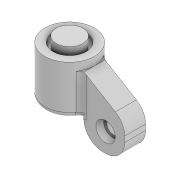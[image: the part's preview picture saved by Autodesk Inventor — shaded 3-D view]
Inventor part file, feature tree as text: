
AUTODESK INVENTOR PART (.ipt)
format: ipt  version: 2022 (Build 260153000, 153)  size: 234,496 bytes
history: native  units: mm
features: extrude x7, sketch x7, projected_geometry x6, fillet x3, plane x1, mirror x1
ambient origin geometry x8: Origin, YZ Plane, XZ Plane, XY Plane, X Axis, Y Axis, Z Axis, Center Point
bodies: Solid1 (feature_tree)
feature tree (25):
  extrude  "Extrusion1"  Depth=12.2mm
  extrude  "Extrusion2"  Depth=3.0mm TaperAngle=0.0deg
  extrude  "Extrusion3"  Depth=3.0mm TaperAngle=0.0deg
  plane  "Work Plane1"
  sketch  "Sketch5"  dims[d11=8.0mm d12=7.0mm d13=7.0mm d14=15.0mm d15=6.0mm]
  extrude  "Extrusion4"  Depth=7.1mm
  mirror  "Mirror2"
  extrude  "Extrusion5"  Depth=7.0mm
  fillet  "Fillet3"  Radius=7.0mm
  fillet  "Fillet4"  Radius=15.0mm
  fillet  "Fillet5"  Radius=6.0mm
  extrude  "Extrusion8"  Depth=100.0mm TaperAngle=0.0deg
  extrude  "Extrusion9"  Depth=3.0mm
  sketch  "Sketch1"  dims[d0=9.8mm d1=12.2mm]
  sketch  "Sketch2"  dims[d2=3.0mm d3=15.0mm d4=0.0mm]
  projected_geometry  "Projected Loop1"
  sketch  "Sketch3"  dims[d5=2.0mm d6=0.0mm d7=3.0mm d8=0.0mm]
  projected_geometry  "Projected Loop2"
  sketch  "Sketch4"  dims[d9=0.0mm d10=7.1mm]
  projected_geometry  "Projected Loop3"
  sketch  "Sketch8"  dims[d16=3.85mm d17=0.0mm d20=100.0mm d21=0.0mm]
  projected_geometry  "Projected Loop5"
  projected_geometry  "Projected Loop6"
  projected_geometry  "Projected Loop7"
  sketch  "Sketch9"  dims[d22=7.0mm d23=3.0mm d24=2.0mm d32=100.0mm d33=0.0mm d34=5.0mm d35=2.0mm d36=0.0mm]
